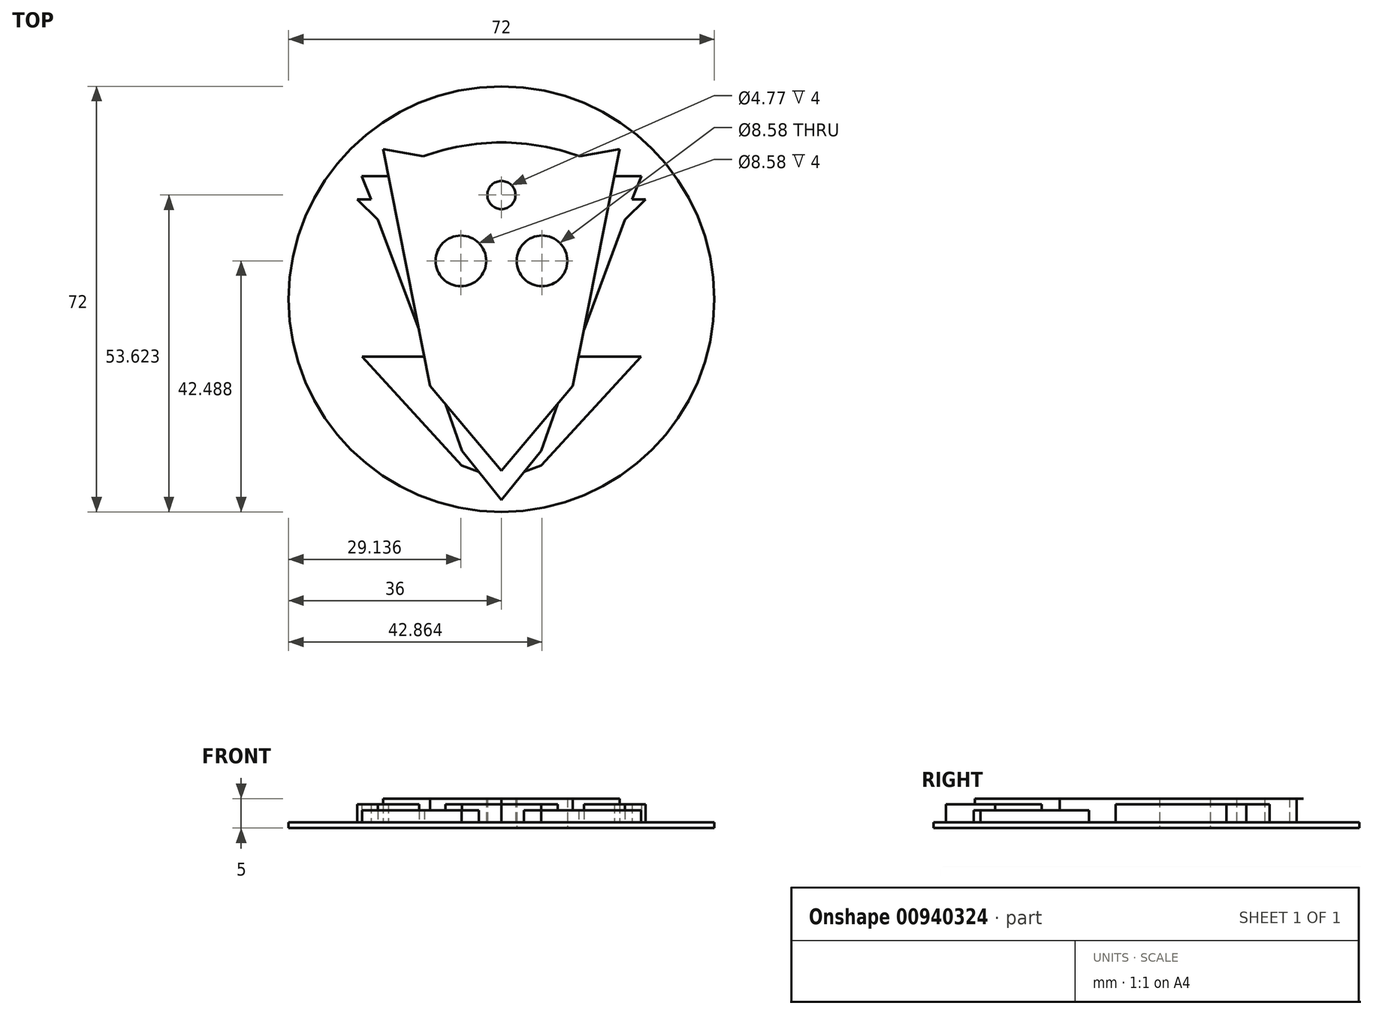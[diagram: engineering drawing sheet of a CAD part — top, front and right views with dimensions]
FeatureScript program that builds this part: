
annotation { "Feature Type Name" : "Feature", "Feature Type Description" : "" }
export const myFeature = defineFeature(function(context is Context, id is Id, definition is map)
    precondition{}
    {
        {
            var Q0;
            Q0=qCreatedBy(makeId("Top.planeOp"),FACE);
            var sketch = newSketch(context, id + "F0", { "sketchPlane" : qUnion([Q0])});
            skLineSegment(sketch, "E0", {"start": v(-12.08, -10.65) * mm, "end": v(-20, 29.41) * mm});
            skLineSegment(sketch, "E1", {"start": v(-20, 29.41) * mm, "end": v(-13.23, 28.16) * mm});
            skLineSegment(sketch, "E2", {"start": v(-13.94, -1.22) * mm, "end": v(-20.89, 17.48) * mm});
            skLineSegment(sketch, "E3", {"start": v(-20.89, 17.48) * mm, "end": v(-24.36, 20.86) * mm});
            skLineSegment(sketch, "E4", {"start": v(-24.36, 20.86) * mm, "end": v(-22.06, 20.86) * mm});
            skLineSegment(sketch, "E5", {"start": v(-22.06, 20.86) * mm, "end": v(-23.65, 24.84) * mm});
            skLineSegment(sketch, "E6", {"start": v(-23.65, 24.84) * mm, "end": v(-19.1, 24.84) * mm});
            skArc(sketch, "E7", {"start": v(0, 30.53) * mm, "mid": v(-6.72, 29.92) * mm, "end": v(-13.23, 28.16) * mm});
            skLineSegment(sketch, "E8", {"start": v(-13.05, -5.72) * mm, "end": v(-23.6, -5.72) * mm});
            skLineSegment(sketch, "E9", {"start": v(-23.6, -5.72) * mm, "end": v(-6.75, -24.12) * mm});
            skLineSegment(sketch, "E10", {"start": v(-6.7, -21.63) * mm, "end": v(0, -29.95) * mm});
            skLineSegment(sketch, "E11", {"start": v(-6.75, -24.12) * mm, "end": v(-3.8, -25.24) * mm});
            skLineSegment(sketch, "E12", {"start": v(0, 30.53) * mm, "end": v(0, 0) * mm, "construction": true});
            skLineSegment(sketch, "E13", {"start": v(0, 0) * mm, "end": v(0, -29.95) * mm, "construction": true});
            skLineSegment(sketch, "E14", {"start": v(-12.08, -10.65) * mm, "end": v(0, -25) * mm});
            skLineSegment(sketch, "E15", {"start": v(-6.7, -21.63) * mm, "end": v(-9.49, -13.73) * mm});
            skLineSegment(sketch, "E16.MirrorCS", {"start": v(24.36, 20.86) * mm, "end": v(22.06, 20.86) * mm});
            skLineSegment(sketch, "E17.MirrorCS", {"start": v(13.05, -5.72) * mm, "end": v(23.6, -5.72) * mm});
            skLineSegment(sketch, "E18.MirrorCS", {"start": v(12.08, -10.65) * mm, "end": v(20, 29.41) * mm});
            skLineSegment(sketch, "E19.MirrorCS", {"start": v(13.94, -1.22) * mm, "end": v(20.89, 17.48) * mm});
            skLineSegment(sketch, "E20.MirrorCS", {"start": v(6.7, -21.63) * mm, "end": v(0, -29.95) * mm});
            skLineSegment(sketch, "E21.MirrorCS", {"start": v(20.89, 17.48) * mm, "end": v(24.36, 20.86) * mm});
            skLineSegment(sketch, "E22.MirrorCS", {"start": v(6.7, -21.63) * mm, "end": v(9.49, -13.73) * mm});
            skLineSegment(sketch, "E23.MirrorCS", {"start": v(20, 29.41) * mm, "end": v(13.23, 28.16) * mm});
            skLineSegment(sketch, "E24.MirrorCS", {"start": v(22.06, 20.86) * mm, "end": v(23.65, 24.84) * mm});
            skLineSegment(sketch, "E25.MirrorCS", {"start": v(23.6, -5.72) * mm, "end": v(6.75, -24.12) * mm});
            skLineSegment(sketch, "E26.MirrorCS", {"start": v(6.75, -24.12) * mm, "end": v(3.8, -25.24) * mm});
            skLineSegment(sketch, "E27.MirrorCS", {"start": v(23.65, 24.84) * mm, "end": v(19.1, 24.84) * mm});
            skLineSegment(sketch, "E28.MirrorCS", {"start": v(12.08, -10.65) * mm, "end": v(0, -25) * mm});
            skArc(sketch, "E29.MirrorCS", {"start": v(0, 30.53) * mm, "mid": v(6.72, 29.92) * mm, "end": v(13.23, 28.16) * mm});
            skCircle(sketch, "E30", {"center": v(-6.86, 10.49) * mm, "radius": 4.29 * mm});
            skCircle(sketch, "E31", {"center": v(0, 21.62) * mm, "radius": 2.38 * mm});
            skCircle(sketch, "E32.MirrorC", {"center": v(6.86, 10.49) * mm, "radius": 4.29 * mm});
            skLineSegment(sketch, "E33", {"start": v(0, 0) * mm, "end": v(0, 4) * mm});
            skCircle(sketch, "E34", {"center": v(0, 4) * mm, "radius": 36 * mm});
            skSolve(sketch);
        }
        {
            var Q0;
            {var subQ9=sQuery(id+"F0.wireOp",EDGE,"E1");Q0=makeQuery(id+"F0.imprint","IMPRINT",FACE,{"disambiguationData":[TD([[makeQuery(id+"F0.imprint","IMPRINT",EDGE,{"derivedFrom":subQ9}),-1.0]])]});}
            extrude(context, id + "F1", {"entities" : qUnion([Q0]), "depth" : 4 * mm, "offsetDistance" : 25 * mm});
        }
        {
            var Q0;
            {var subQ3=sQuery(id+"F0.wireOp",EDGE,"E8");Q0=makeQuery(id+"F0.imprint","IMPRINT",FACE,{"disambiguationData":[TD([[makeQuery(id+"F0.imprint","IMPRINT",EDGE,{"derivedFrom":subQ3}),1.0]])]});}
            var Q1;
            {var subQ4=sQuery(id+"F0.wireOp",EDGE,"E17.MirrorCS");Q1=makeQuery(id+"F0.imprint","IMPRINT",FACE,{"disambiguationData":[TD([[makeQuery(id+"F0.imprint","IMPRINT",EDGE,{"derivedFrom":subQ4}),-1.0]])]});}
            extrude(context, id + "F2", {"entities" : qUnion([Q0, Q1]), "operationType" : NewBodyOperationType.ADD, "depth" : 2 * mm, "offsetDistance" : 25 * mm});
        }
        {
            var Q0;
            {var subQ3=sQuery(id+"F0.wireOp",EDGE,"E15");Q0=makeQuery(id+"F0.imprint","IMPRINT",FACE,{"disambiguationData":[TD([[makeQuery(id+"F0.imprint","IMPRINT",EDGE,{"derivedFrom":subQ3}),-1.0]])]});}
            var Q1;
            {var subQ0=sQuery(id+"F0.wireOp",EDGE,"E2");Q1=makeQuery(id+"F0.imprint","IMPRINT",FACE,{"disambiguationData":[TD([[makeQuery(id+"F0.imprint","IMPRINT",EDGE,{"derivedFrom":subQ0}),-1.0]])]});}
            var Q2;
            Q2=makeQuery(id+"F0.imprint","IMPRINT",FACE,{"disambiguationData":[TD([[makeQuery(id+"F0.imprint","IMPRINT",EDGE,{"derivedFrom":sQuery(id+"F0.wireOp",EDGE,"E16.MirrorCS")}),1.0]])]});
            extrude(context, id + "F3", {"entities" : qUnion([Q0, Q1, Q2]), "operationType" : NewBodyOperationType.ADD, "depth" : 3 * mm, "offsetDistance" : 25 * mm});
        }
        {
            var Q0;
            {var subQ0=sQuery(id+"F0.wireOp",EDGE,"E2");Q0=makeQuery(id+"F0.imprint","IMPRINT",FACE,{"disambiguationData":[TD([[makeQuery(id+"F0.imprint","IMPRINT",EDGE,{"derivedFrom":subQ0}),1.0]])]});}
            var Q1;
            {var subQ5=sQuery(id+"F0.wireOp",EDGE,"E17.MirrorCS");Q1=makeQuery(id+"F0.imprint","IMPRINT",FACE,{"disambiguationData":[TD([[makeQuery(id+"F0.imprint","IMPRINT",EDGE,{"derivedFrom":subQ5}),1.0]])]});}
            var Q2;
            Q2=makeQuery(id+"F0.imprint","IMPRINT",FACE,{"disambiguationData":[TD([[makeQuery(id+"F0.imprint","IMPRINT",EDGE,{"derivedFrom":sQuery(id+"F0.wireOp",EDGE,"E16.MirrorCS")}),-1.0]])]});
            var Q3;
            {var subQ0=sQuery(id+"F0.wireOp",EDGE,"E1");Q3=makeQuery(id+"F0.imprint","IMPRINT",FACE,{"disambiguationData":[TD([[makeQuery(id+"F0.imprint","IMPRINT",EDGE,{"derivedFrom":subQ0}),1.0]])]});}
            var Q4;
            Q4=makeQuery(id+"F0.imprint","IMPRINT",FACE,{"disambiguationData":[TD([[makeQuery(id+"F0.imprint","IMPRINT",EDGE,{"derivedFrom":sQuery(id+"F0.wireOp",EDGE,"E30")}),1.0]])]});
            var Q5;
            Q5=makeQuery(id+"F0.imprint","IMPRINT",FACE,{"disambiguationData":[TD([[makeQuery(id+"F0.imprint","IMPRINT",EDGE,{"derivedFrom":sQuery(id+"F0.wireOp",EDGE,"E32.MirrorC")}),-1.0]])]});
            var Q6;
            Q6=makeQuery(id+"F0.imprint","IMPRINT",FACE,{"disambiguationData":[TD([[makeQuery(id+"F0.imprint","IMPRINT",EDGE,{"derivedFrom":sQuery(id+"F0.wireOp",EDGE,"E31")}),1.0]])]});
            var Q7;
            {var subQ3=sQuery(id+"F0.wireOp",EDGE,"E8");Q7=makeQuery(id+"F0.imprint","IMPRINT",FACE,{"disambiguationData":[TD([[makeQuery(id+"F0.imprint","IMPRINT",EDGE,{"derivedFrom":subQ3}),1.0]])]});}
            var Q8;
            {var subQ4=sQuery(id+"F0.wireOp",EDGE,"E17.MirrorCS");Q8=makeQuery(id+"F0.imprint","IMPRINT",FACE,{"disambiguationData":[TD([[makeQuery(id+"F0.imprint","IMPRINT",EDGE,{"derivedFrom":subQ4}),-1.0]])]});}
            var Q9;
            {var subQ3=sQuery(id+"F0.wireOp",EDGE,"E15");Q9=makeQuery(id+"F0.imprint","IMPRINT",FACE,{"disambiguationData":[TD([[makeQuery(id+"F0.imprint","IMPRINT",EDGE,{"derivedFrom":subQ3}),-1.0]])]});}
            var Q10;
            {var subQ9=sQuery(id+"F0.wireOp",EDGE,"E1");Q10=makeQuery(id+"F0.imprint","IMPRINT",FACE,{"disambiguationData":[TD([[makeQuery(id+"F0.imprint","IMPRINT",EDGE,{"derivedFrom":subQ9}),-1.0]])]});}
            var Q11;
            {var subQ0=sQuery(id+"F0.wireOp",EDGE,"E2");Q11=makeQuery(id+"F0.imprint","IMPRINT",FACE,{"disambiguationData":[TD([[makeQuery(id+"F0.imprint","IMPRINT",EDGE,{"derivedFrom":subQ0}),-1.0]])]});}
            var Q12;
            Q12=makeQuery(id+"F0.imprint","IMPRINT",FACE,{"disambiguationData":[TD([[makeQuery(id+"F0.imprint","IMPRINT",EDGE,{"derivedFrom":sQuery(id+"F0.wireOp",EDGE,"E16.MirrorCS")}),1.0]])]});
            extrude(context, id + "F4", {"entities" : qUnion([Q0, Q1, Q2, Q3, Q4, Q5, Q6, Q7, Q8, Q9, Q10, Q11, Q12]), "operationType" : NewBodyOperationType.ADD, "oppositeDirection" : true, "depth" : 1 * mm, "offsetDistance" : 25 * mm});
        }
    });
